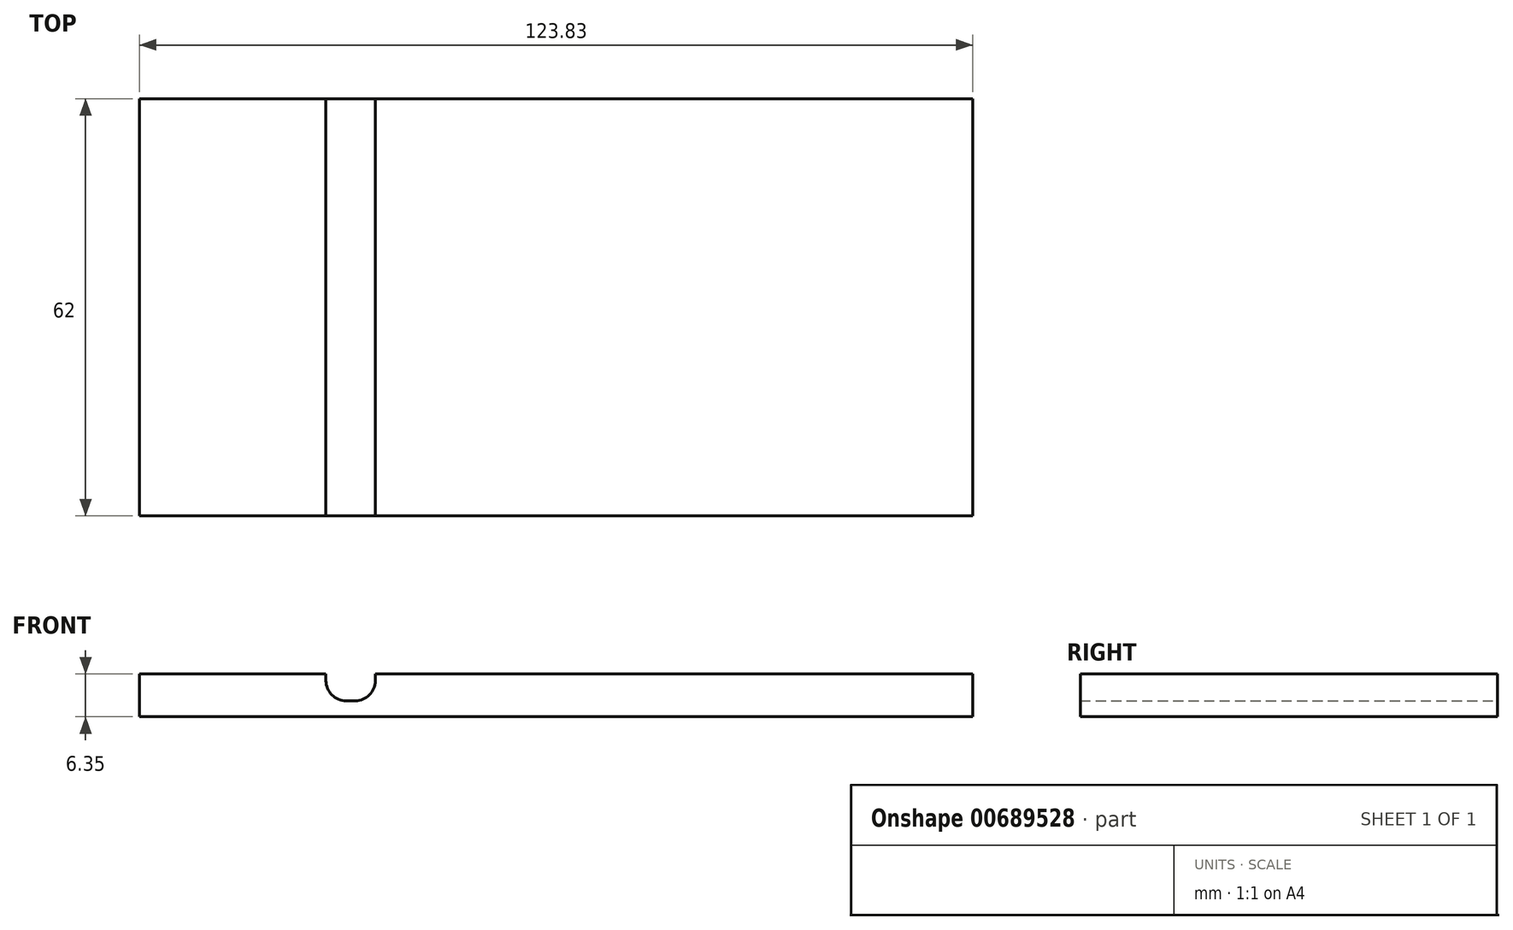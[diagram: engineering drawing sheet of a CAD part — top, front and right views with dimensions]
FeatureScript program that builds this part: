
annotation { "Feature Type Name" : "Feature", "Feature Type Description" : "" }
export const myFeature = defineFeature(function(context is Context, id is Id, definition is map)
    precondition{}
    {
        {
            var Q0;
            Q0=qCreatedBy(makeId("Front.planeOp"),FACE);
            var sketch = newSketch(context, id + "F0", { "sketchPlane" : qUnion([Q0])});
            skLineSegment(sketch, "E0.bottom", {"start": v(-31.75, 73.61) * mm, "end": v(-4.02, 73.61) * mm});
            skLineSegment(sketch, "E0.top", {"start": v(-31.75, 67.26) * mm, "end": v(92.08, 67.26) * mm});
            skLineSegment(sketch, "E0.left", {"start": v(-31.75, 73.61) * mm, "end": v(-31.75, 67.26) * mm});
            skLineSegment(sketch, "E0.right", {"start": v(92.08, 73.61) * mm, "end": v(92.08, 67.26) * mm});
            skLineSegment(sketch, "E1.bottom", {"start": v(-4.02, 72.61) * mm, "end": v(3.32, 72.61) * mm});
            skLineSegment(sketch, "E1.top", {"start": v(-4.02, 79.17) * mm, "end": v(3.32, 79.17) * mm});
            skLineSegment(sketch, "E1.left", {"start": v(-4.02, 72.61) * mm, "end": v(-4.02, 73.61) * mm});
            skLineSegment(sketch, "E1.right", {"start": v(3.32, 72.61) * mm, "end": v(3.32, 73.61) * mm});
            skLineSegment(sketch, "E2.bottom", {"start": v(-1.02, 69.61) * mm, "end": v(-1.02, 69.61) * mm});
            skLineSegment(sketch, "E2.top", {"start": v(-1.02, 72.61) * mm, "end": v(0.32, 72.61) * mm});
            skLineSegment(sketch, "E2.left", {"start": v(-1.02, 69.61) * mm, "end": v(-1.02, 72.61) * mm});
            skLineSegment(sketch, "E2.right", {"start": v(0.32, 69.61) * mm, "end": v(0.32, 72.61) * mm});
            skLineSegment(sketch, "E3", {"start": v(3.32, 73.61) * mm, "end": v(3.32, 79.17) * mm});
            skLineSegment(sketch, "E4", {"start": v(-4.02, 73.61) * mm, "end": v(-4.02, 79.17) * mm});
            skLineSegment(sketch, "E5", {"start": v(-1.02, 69.61) * mm, "end": v(0.32, 69.61) * mm});
            skLineSegment(sketch, "E6", {"start": v(3.32, 73.61) * mm, "end": v(3.32, 73.61) * mm});
            skLineSegment(sketch, "E7", {"start": v(-4.02, 73.61) * mm, "end": v(-3.85, 73.61) * mm});
            skArc(sketch, "E8", {"start": v(-1.02, 69.61) * mm, "mid": v(1.43, 74.35) * mm, "end": v(-3.85, 73.61) * mm});
            skArc(sketch, "E9", {"start": v(-4.02, 72.61) * mm, "mid": v(-3.14, 70.5) * mm, "end": v(-1.02, 69.61) * mm});
            skArc(sketch, "E10", {"start": v(0.26, 69.61) * mm, "mid": v(2.42, 70.47) * mm, "end": v(3.32, 72.61) * mm});
            skArc(sketch, "E11", {"start": v(3.32, 72.61) * mm, "mid": v(3.28, 73.12) * mm, "end": v(3.15, 73.61) * mm});
            skLineSegment(sketch, "E12", {"start": v(3.32, 73.61) * mm, "end": v(92.08, 73.61) * mm});
            skArc(sketch, "E13", {"start": v(-3.86, 73.59) * mm, "mid": v(-3.98, 73.1) * mm, "end": v(-4.02, 72.61) * mm});
            skArc(sketch, "E14", {"start": v(3.15, 73.61) * mm, "mid": v(-2.1, 74.37) * mm, "end": v(0.26, 69.61) * mm});
            skLineSegment(sketch, "E15", {"start": v(-3.85, 73.61) * mm, "end": v(3.15, 73.61) * mm});
            skLineSegment(sketch, "E16", {"start": v(3.15, 73.61) * mm, "end": v(3.32, 73.61) * mm});
            skArc(sketch, "E17", {"start": v(-3.85, 73.61) * mm, "mid": v(-3.86, 73.6) * mm, "end": v(-3.86, 73.59) * mm});
            skPoint(sketch, "E18", {"position": v(-0.35, 75.54) * mm});
            skSolve(sketch);
        }
        {
            var Q0;
            Q0=makeQuery(id+"F0.imprint","IMPRINT",FACE,{"disambiguationData":[TD([[makeQuery(id+"F0.imprint","IMPRINT",EDGE,{"derivedFrom":sQuery(id+"F0.wireOp",EDGE,"E0.bottom")}),-1.0]])]});
            extrude(context, id + "F1", {"entities" : qUnion([Q0]), "depth" : 62 * mm, "offsetDistance" : 25.4 * mm});
        }
    });
